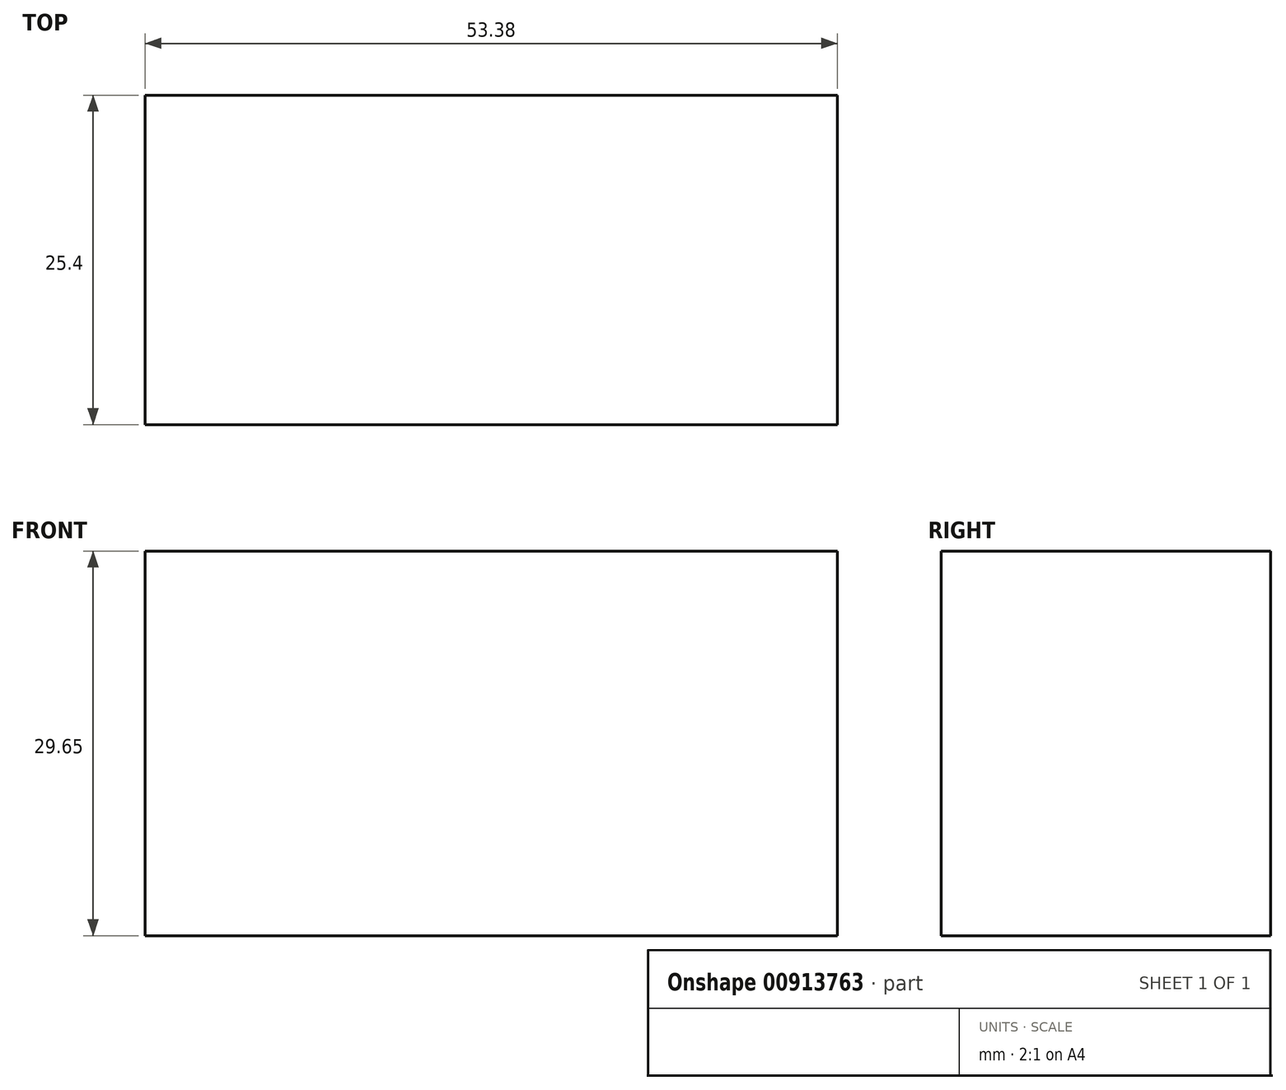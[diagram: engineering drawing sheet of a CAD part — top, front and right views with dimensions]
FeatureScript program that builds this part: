
annotation { "Feature Type Name" : "Feature", "Feature Type Description" : "" }
export const myFeature = defineFeature(function(context is Context, id is Id, definition is map)
    precondition{}
    {
        {
            var Q0;
            Q0=qCreatedBy(makeId("Front.planeOp"),FACE);
            var sketch = newSketch(context, id + "F0", { "sketchPlane" : qUnion([Q0])});
            skLineSegment(sketch, "E0.bottom", {"start": v(0, 0) * mm, "end": v(-53.38, 0) * mm});
            skLineSegment(sketch, "E0.top", {"start": v(0, 29.65) * mm, "end": v(-53.38, 29.65) * mm});
            skLineSegment(sketch, "E0.left", {"start": v(0, 0) * mm, "end": v(0, 29.65) * mm});
            skLineSegment(sketch, "E0.right", {"start": v(-53.38, 0) * mm, "end": v(-53.38, 29.65) * mm});
            skSolve(sketch);
        }
        {
            var Q0;
            Q0=makeQuery(id+"F0.imprint","IMPRINT",FACE,{"disambiguationData":[TD([[makeQuery(id+"F0.imprint","IMPRINT",EDGE,{"derivedFrom":sQuery(id+"F0.wireOp",EDGE,"E0.bottom")}),-1.0]])]});
            extrude(context, id + "F1", {"entities" : qUnion([Q0]), "depth" : 25.4 * mm, "offsetDistance" : 25.4 * mm});
        }
    });
